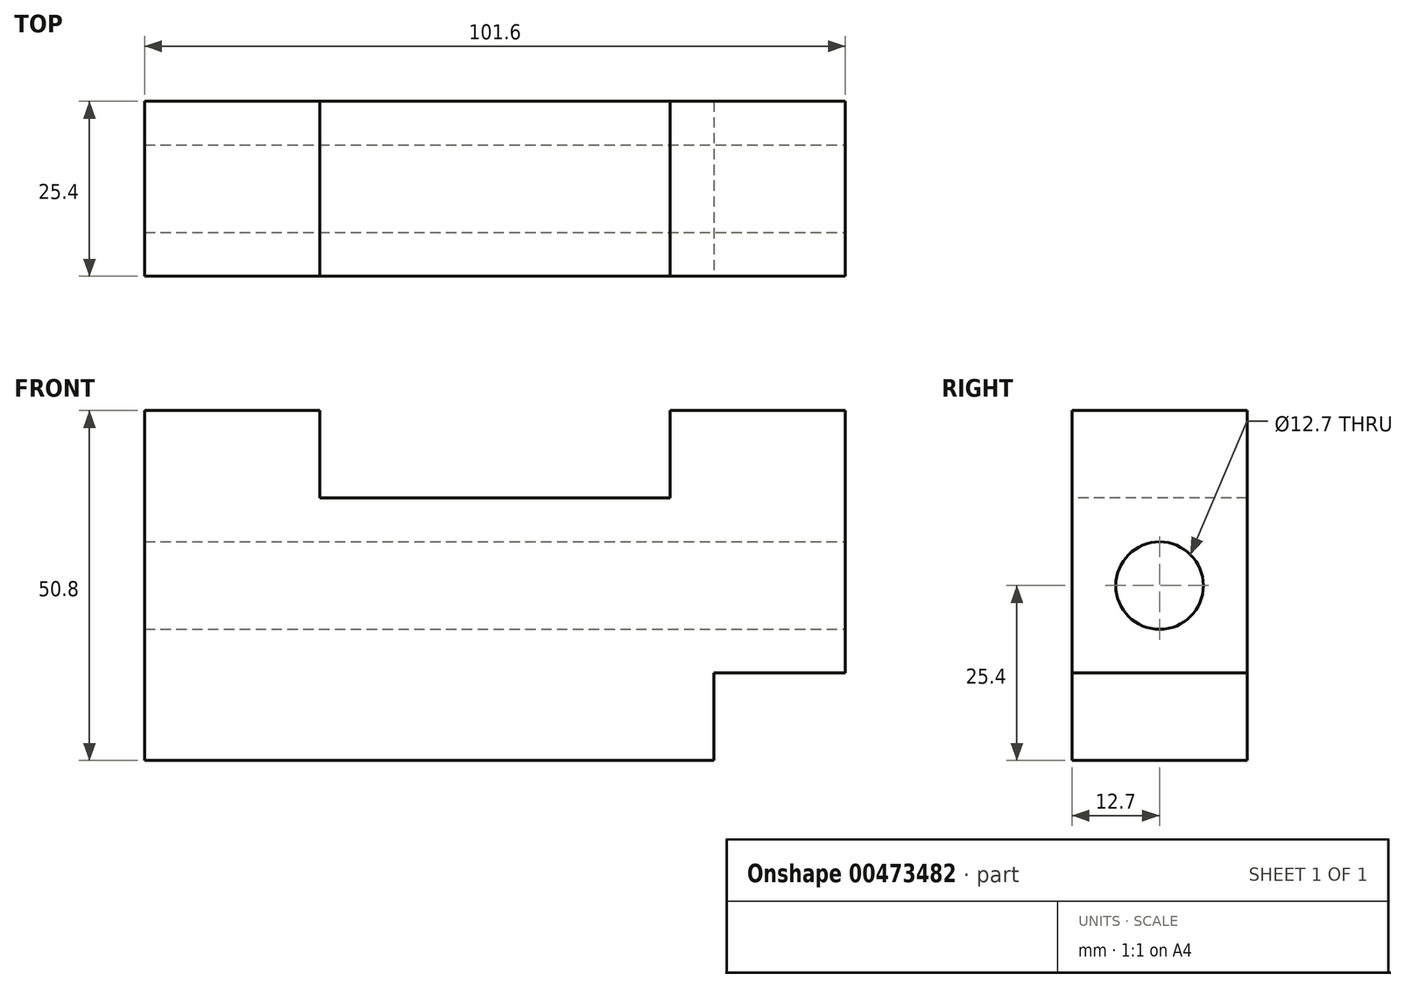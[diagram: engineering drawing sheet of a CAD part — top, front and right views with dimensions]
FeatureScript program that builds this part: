
annotation { "Feature Type Name" : "Feature", "Feature Type Description" : "" }
export const myFeature = defineFeature(function(context is Context, id is Id, definition is map)
    precondition{}
    {
        {
            var Q0;
            Q0=qCreatedBy(makeId("Front.planeOp"),FACE);
            var sketch = newSketch(context, id + "F0", { "sketchPlane" : qUnion([Q0])});
            skLineSegment(sketch, "E0.bottom", {"start": v(-50.8, 25.4) * mm, "end": v(50.8, 25.4) * mm});
            skLineSegment(sketch, "E0.top", {"start": v(-50.8, -25.4) * mm, "end": v(50.8, -25.4) * mm});
            skLineSegment(sketch, "E0.left", {"start": v(-50.8, 25.4) * mm, "end": v(-50.8, -25.4) * mm});
            skLineSegment(sketch, "E0.right", {"start": v(50.8, 25.4) * mm, "end": v(50.8, -25.4) * mm});
            skPoint(sketch, "E0.middle", {"position": v(0, 0) * mm});
            skSolve(sketch);
        }
        {
            var Q0;
            Q0=makeQuery(id+"F0.imprint","IMPRINT",FACE,{"disambiguationData":[TD([[makeQuery(id+"F0.imprint","IMPRINT",EDGE,{"derivedFrom":sQuery(id+"F0.wireOp",EDGE,"E0.bottom")}),-1.0]])]});
            extrude(context, id + "F1", {"entities" : qUnion([Q0]), "depth" : 25.4 * mm});
        }
        {
            var Q0;
            Q0=makeQuery(id+"F1.opExtrude","CAP_FACE",FACE,{"disambiguationData":[OSD([sQuery(id+"F0.wireOp",EDGE,"E0.bottom"),sQuery(id+"F0.wireOp",EDGE,"E0.top"),sQuery(id+"F0.wireOp",EDGE,"E0.left"),sQuery(id+"F0.wireOp",EDGE,"E0.right")])],"isStart":false});
            var sketch = newSketch(context, id + "F2", { "sketchPlane" : qUnion([Q0])});
            skLineSegment(sketch, "E1.bottom", {"start": v(-25.4, 25.4) * mm, "end": v(25.4, 25.4) * mm});
            skLineSegment(sketch, "E1.top", {"start": v(-25.4, 12.7) * mm, "end": v(25.4, 12.7) * mm});
            skLineSegment(sketch, "E1.left", {"start": v(-25.4, 25.4) * mm, "end": v(-25.4, 12.7) * mm});
            skLineSegment(sketch, "E1.right", {"start": v(25.4, 25.4) * mm, "end": v(25.4, 12.7) * mm});
            skSolve(sketch);
        }
        {
            var Q0;
            Q0=makeQuery(id+"F2.imprint","IMPRINT",FACE,{"disambiguationData":[TD([[makeQuery(id+"F2.imprint","IMPRINT",EDGE,{"derivedFrom":sQuery(id+"F2.wireOp",EDGE,"E1.bottom")}),-1.0]])]});
            extrude(context, id + "F3", {"entities" : qUnion([Q0]), "operationType" : NewBodyOperationType.REMOVE, "oppositeDirection" : true, "depth" : 25.4 * mm});
        }
        {
            var Q0;
            Q0=makeQuery(id+"F1.opExtrude","CAP_FACE",FACE,{"disambiguationData":[OSD([sQuery(id+"F0.wireOp",EDGE,"E0.bottom"),sQuery(id+"F0.wireOp",EDGE,"E0.top"),sQuery(id+"F0.wireOp",EDGE,"E0.left"),sQuery(id+"F0.wireOp",EDGE,"E0.right")])],"isStart":false});
            var sketch = newSketch(context, id + "F4", { "sketchPlane" : qUnion([Q0])});
            skLineSegment(sketch, "E2.bottom", {"start": v(50.8, -12.7) * mm, "end": v(31.75, -12.7) * mm});
            skLineSegment(sketch, "E2.top", {"start": v(50.8, -25.4) * mm, "end": v(31.75, -25.4) * mm});
            skLineSegment(sketch, "E2.left", {"start": v(50.8, -12.7) * mm, "end": v(50.8, -25.4) * mm});
            skLineSegment(sketch, "E2.right", {"start": v(31.75, -12.7) * mm, "end": v(31.75, -25.4) * mm});
            skSolve(sketch);
        }
        {
            var Q0;
            Q0=makeQuery(id+"F4.imprint","IMPRINT",FACE,{"disambiguationData":[TD([[makeQuery(id+"F4.imprint","IMPRINT",EDGE,{"derivedFrom":sQuery(id+"F4.wireOp",EDGE,"E2.bottom")}),1.0]])]});
            extrude(context, id + "F5", {"entities" : qUnion([Q0]), "operationType" : NewBodyOperationType.REMOVE, "oppositeDirection" : true, "depth" : 25.4 * mm});
        }
        {
            var Q0;
            Q0=makeQuery(id+"F1.opExtrude","SWEPT_FACE",FACE,{"disambiguationData":[OSD([sQuery(id+"F0.wireOp",EDGE,"E0.right")])]});
            var sketch = newSketch(context, id + "F6", { "sketchPlane" : qUnion([Q0])});
            skCircle(sketch, "E3", {"center": v(-12.7, 0) * mm, "radius": 6.35 * mm});
            skSolve(sketch);
        }
        {
            var Q0;
            Q0=makeQuery(id+"F6.imprint","IMPRINT",FACE,{"disambiguationData":[TD([[makeQuery(id+"F6.imprint","IMPRINT",EDGE,{"derivedFrom":sQuery(id+"F6.wireOp",EDGE,"E3")}),1.0]])]});
            extrude(context, id + "F7", {"entities" : qUnion([Q0]), "operationType" : NewBodyOperationType.REMOVE, "endBound" : BoundingType.THROUGH_ALL, "oppositeDirection" : true, "depth" : 25.4 * mm});
        }
    });
